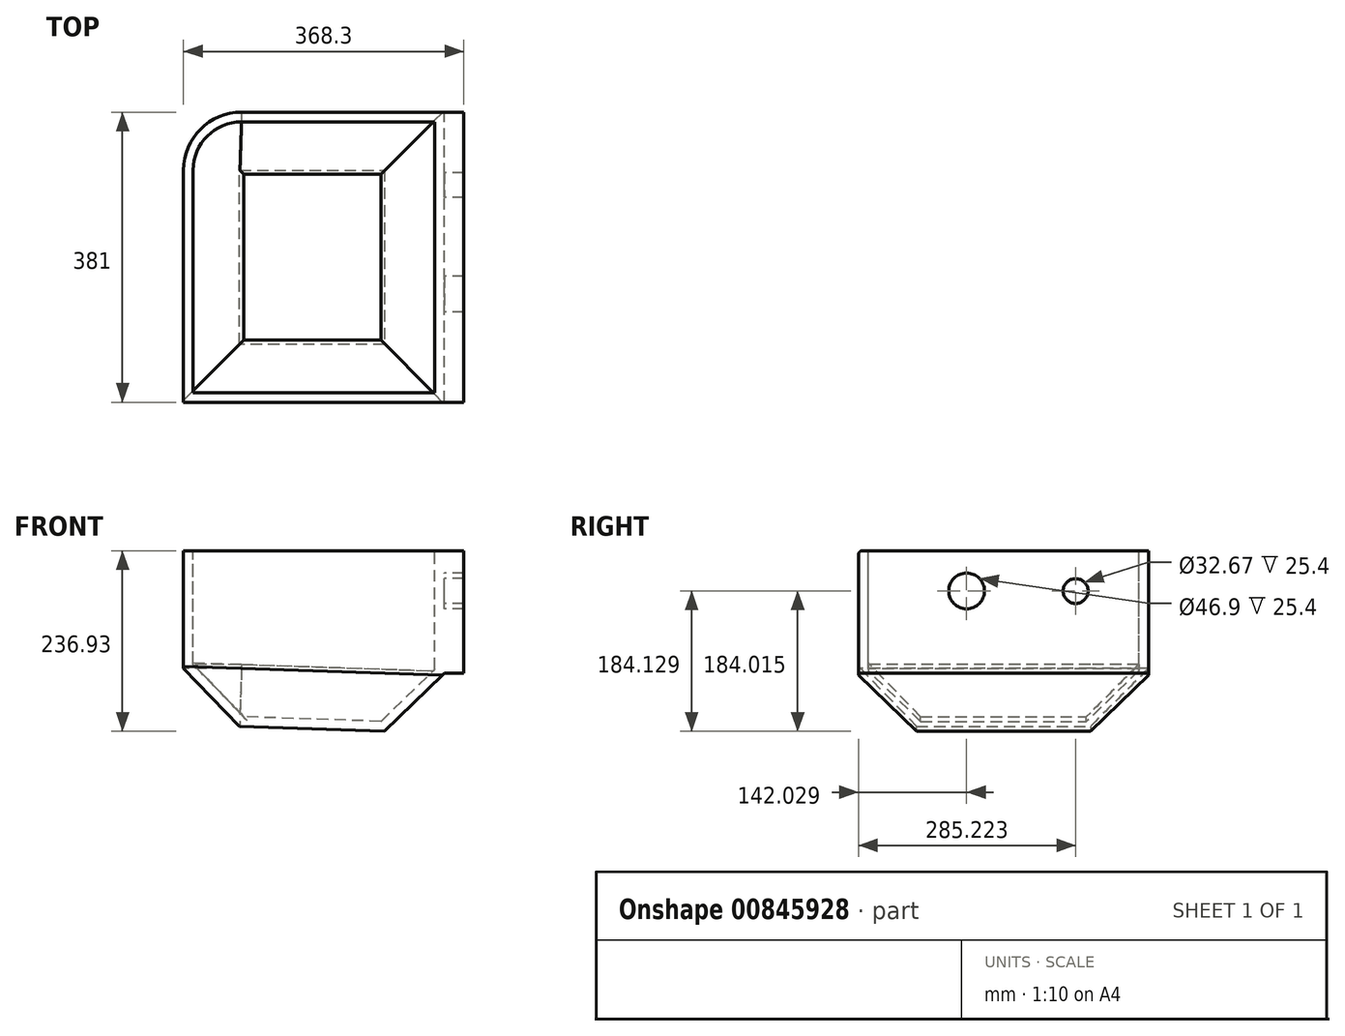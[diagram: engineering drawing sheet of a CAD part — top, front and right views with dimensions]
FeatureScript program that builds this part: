
annotation { "Feature Type Name" : "Feature", "Feature Type Description" : "" }
export const myFeature = defineFeature(function(context is Context, id is Id, definition is map)
    precondition{}
    {
        {
            var Q0;
            Q0=qCreatedBy(makeId("Front.planeOp"),FACE);
            var sketch = newSketch(context, id + "F0", { "sketchPlane" : qUnion([Q0])});
            skLineSegment(sketch, "E0.bottom", {"start": v(-175.41, -181.09) * mm, "end": v(167.49, -181.09) * mm});
            skLineSegment(sketch, "E0.top", {"start": v(-175.41, 199.91) * mm, "end": v(167.49, 199.91) * mm});
            skLineSegment(sketch, "E0.left", {"start": v(-175.41, -28.24) * mm, "end": v(-175.41, 199.91) * mm});
            skLineSegment(sketch, "E0.right", {"start": v(167.49, -39.63) * mm, "end": v(167.49, 199.91) * mm});
            skLineSegment(sketch, "E1", {"start": v(-175.41, -28.24) * mm, "end": v(167.49, -39.63) * mm});
            skSolve(sketch);
        }
        {
            var Q0;
            Q0=makeQuery(id+"F0.imprint","IMPRINT",FACE,{"disambiguationData":[TD([[makeQuery(id+"F0.imprint","IMPRINT",EDGE,{"derivedFrom":sQuery(id+"F0.wireOp",EDGE,"E0.top")}),-1.0]])]});
            extrude(context, id + "F1", {"entities" : qUnion([Q0]), "depth" : 381 * mm, "offsetDistance" : 25.4 * mm});
        }
        {
            var Q0;
            Q0=makeQuery(id+"F1.opExtrude","CAP_EDGE",EDGE,{"disambiguationData":[OSD([sQuery(id+"F0.wireOp",EDGE,"E0.left")])],"isStart":true});
            fillet(context, id + "F2", {"entities" : qUnion([Q0]), "radius" : 76.2 * mm, "tangentPropagation" : true, "allowEdgeOverflow" : false});
        }
        {
            var Q0;
            Q0=makeQuery(id+"F1.opExtrude","SWEPT_FACE",FACE,{"disambiguationData":[OSD([sQuery(id+"F0.wireOp",EDGE,"E1")])]});
            chamfer(context, id + "F3", {"entities" : qUnion([Q0]), "width" : 76.2 * mm, "tangentPropagation" : true});
        }
        {
            var Q0;
            Q0=makeQuery(id+"F1.opExtrude","SWEPT_FACE",FACE,{"disambiguationData":[OSD([sQuery(id+"F0.wireOp",EDGE,"E0.top")])]});
            shell(context, id + "F4", {"entities" : qUnion([Q0]), "thickness" : 12.7 * mm});
        }
        {
            var Q0;
            Q0=makeQuery(id+"F1.opExtrude","CAP_EDGE",EDGE,{"disambiguationData":[OSD([sQuery(id+"F0.wireOp",EDGE,"E0.top")])],"isStart":false});
            fillet(context, id + "F5", {"entities" : qUnion([Q0]), "radius" : 5.08 * mm, "tangentPropagation" : true, "allowEdgeOverflow" : false});
        }
        {
            var Q0;
            Q0=makeQuery(id+"F1.opExtrude","SWEPT_FACE",FACE,{"disambiguationData":[OSD([sQuery(id+"F0.wireOp",EDGE,"E0.right")])]});
            var sketch = newSketch(context, id + "F6", { "sketchPlane" : qUnion([Q0])});
            skCircle(sketch, "E2", {"center": v(-238.97, 147.1) * mm, "radius": 23.45 * mm});
            skCircle(sketch, "E3", {"center": v(-95.78, 147) * mm, "radius": 16.33 * mm});
            skSolve(sketch);
        }
        {
            var Q0;
            Q0=makeQuery(id+"F6.imprint","IMPRINT",FACE,{"disambiguationData":[TD([[makeQuery(id+"F6.imprint","IMPRINT",EDGE,{"derivedFrom":sQuery(id+"F6.wireOp",EDGE,"E2")}),-1.0]])]});
            extrude(context, id + "F7", {"entities" : qUnion([Q0]), "operationType" : NewBodyOperationType.ADD, "depth" : 25.4 * mm, "offsetDistance" : 25.4 * mm});
        }
    });
